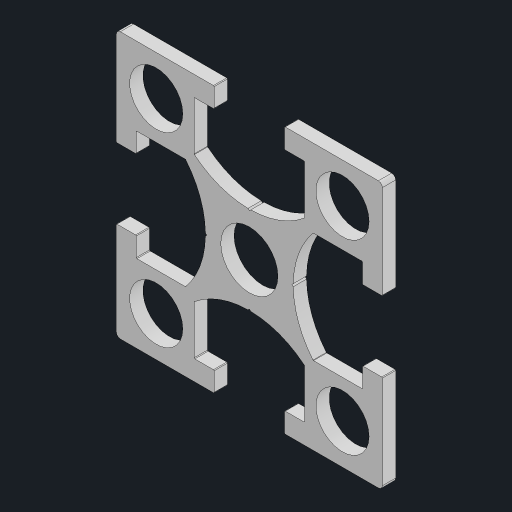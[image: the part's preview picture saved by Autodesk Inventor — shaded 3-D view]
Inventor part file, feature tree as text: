
AUTODESK INVENTOR PART (.ipt)
format: ipt  version: 2024.2 (Build 282272000, 272)  size: 324,608 bytes
history: native  units: mm
features: other x1, extrude x1, fillet x1, sketch x1
ambient origin geometry x8: Origin, YZ Plane, XZ Plane, XY Plane, X Axis, Y Axis, Z Axis, Center Point
bodies: Body1 (feature_tree)
feature tree (4):
  other  "솔리드1"
  extrude  "프로파일 길이 설정"  Depth=20.0mm
  fillet  "모서리"  Radius=20.0mm
  sketch  "스케치1"
